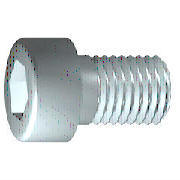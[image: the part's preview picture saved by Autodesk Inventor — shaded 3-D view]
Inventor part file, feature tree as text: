
AUTODESK INVENTOR PART (.ipt)
format: ipt  version: 2021.2 (Build 252289000, 289)  size: 188,928 bytes
history: native  units: mm (DEFAULTED — no unit token found)
features: sketch x2, other x1, extrude x1, plane x1, fillet x1
ambient origin geometry x7: Origin, YZ Plane, XY Plane, X Axis, Y Axis, Z Axis, Center Point
bodies: Solid1 (feature_tree)
feature tree (6):
  other  "Базовый элемент"
  extrude  "Паз"  Depth=20.0mm
  plane  "Work Plane1"
  fillet  "Fillet2"  Radius=0.429515mm
  sketch  "Эскиз1"
  sketch  "Эскиз2"
